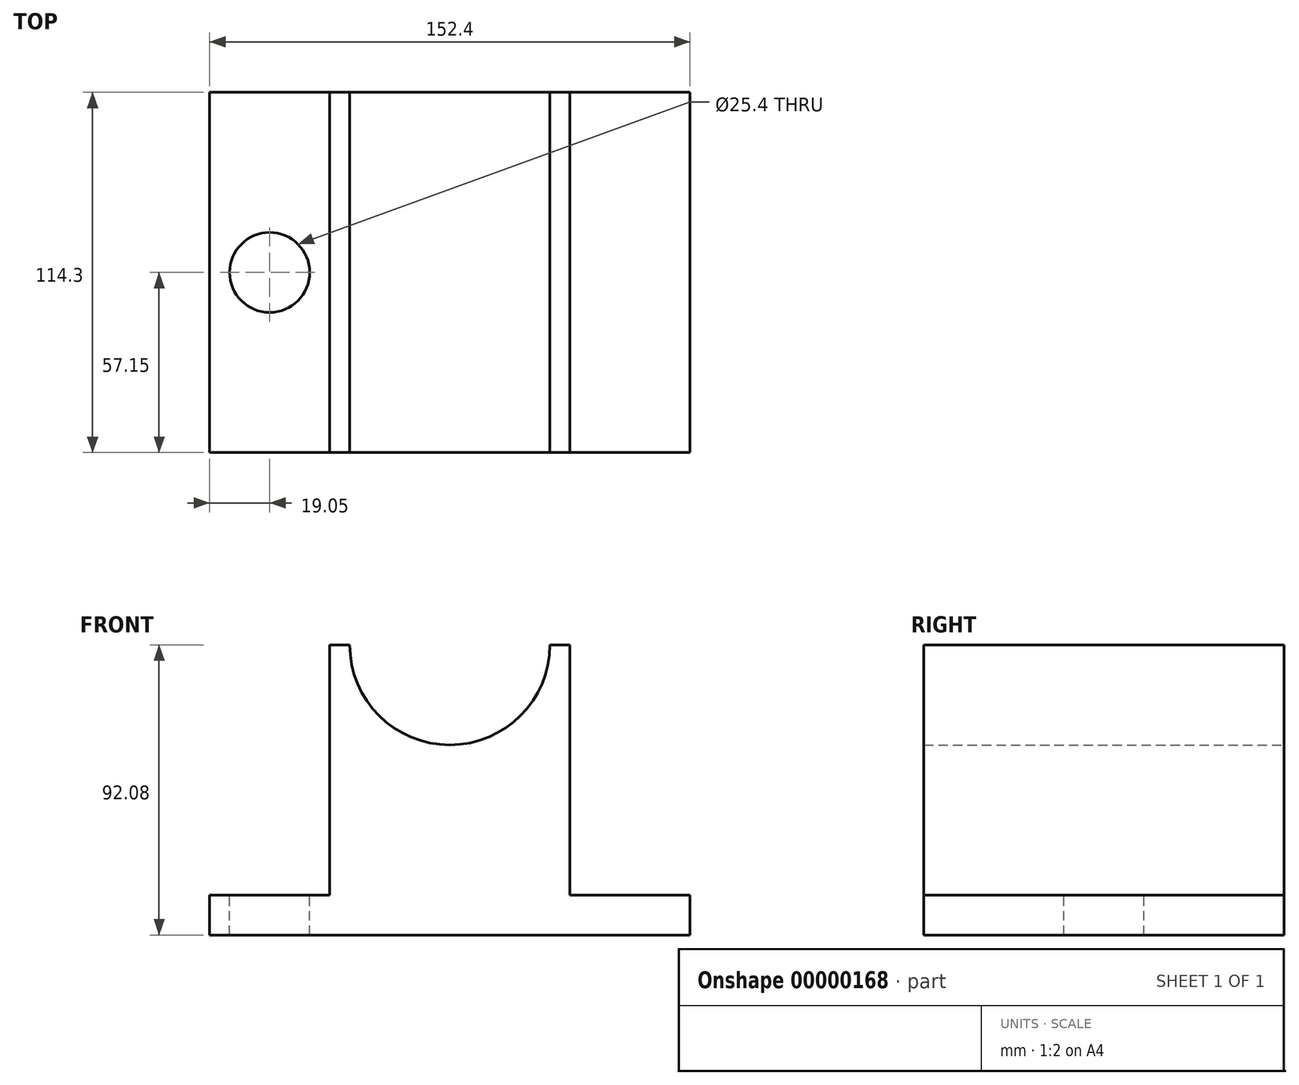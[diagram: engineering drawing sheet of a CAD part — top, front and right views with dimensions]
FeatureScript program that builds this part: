
annotation { "Feature Type Name" : "Feature", "Feature Type Description" : "" }
export const myFeature = defineFeature(function(context is Context, id is Id, definition is map)
    precondition{}
    {
        {
            var Q0;
            Q0=qCreatedBy(makeId("Front.planeOp"),FACE);
            var sketch = newSketch(context, id + "F0", { "sketchPlane" : qUnion([Q0])});
            skLineSegment(sketch, "E0", {"start": v(0, 0) * mm, "end": v(0, 12.7) * mm});
            skLineSegment(sketch, "E1", {"start": v(0, 12.7) * mm, "end": v(38.1, 12.7) * mm});
            skLineSegment(sketch, "E2", {"start": v(38.1, 12.7) * mm, "end": v(38.1, 92.08) * mm});
            skLineSegment(sketch, "E3", {"start": v(38.1, 92.08) * mm, "end": v(44.45, 92.08) * mm});
            skLineSegment(sketch, "E4", {"start": v(114.3, 92.08) * mm, "end": v(114.3, 12.7) * mm});
            skLineSegment(sketch, "E5", {"start": v(114.3, 12.7) * mm, "end": v(152.4, 12.7) * mm});
            skLineSegment(sketch, "E6", {"start": v(152.4, 12.7) * mm, "end": v(152.4, 0) * mm});
            skLineSegment(sketch, "E7", {"start": v(152.4, 0) * mm, "end": v(0, 0) * mm});
            skArc(sketch, "E8", {"start": v(44.45, 92.08) * mm, "mid": v(76.2, 60.33) * mm, "end": v(107.95, 92.08) * mm});
            skLineSegment(sketch, "E9.trimOffspring", {"start": v(107.95, 92.08) * mm, "end": v(114.3, 92.08) * mm});
            skSolve(sketch);
        }
        {
            var Q0;
            Q0=makeQuery(id+"F0.imprint","IMPRINT",FACE,{"disambiguationData":[TD([[makeQuery(id+"F0.imprint","IMPRINT",EDGE,{"derivedFrom":sQuery(id+"F0.wireOp",EDGE,"E0")}),-1.0]])]});
            extrude(context, id + "F1", {"entities" : qUnion([Q0]), "depth" : 114.3 * mm});
        }
        {
            var Q0;
            Q0=makeQuery(id+"F1.opExtrude","SWEPT_FACE",FACE,{"disambiguationData":[OSD([sQuery(id+"F0.wireOp",EDGE,"E1")])]});
            var sketch = newSketch(context, id + "F2", { "sketchPlane" : qUnion([Q0])});
            skCircle(sketch, "E10", {"center": v(19.05, -57.15) * mm, "radius": 12.7 * mm});
            skLineSegment(sketch, "E11.0", {"start": v(107.95, 0) * mm, "end": v(44.45, 0) * mm, "construction": true});
            skLineSegment(sketch, "E12.0", {"start": v(107.95, -114.3) * mm, "end": v(44.45, -114.3) * mm});
            skCircle(sketch, "E13.0.MirrorC", {"center": v(133.35, -57.15) * mm, "radius": 12.7 * mm});
            skSolve(sketch);
        }
        {
            var Q0;
            Q0=makeQuery(id+"F2.imprint","IMPRINT",FACE,{"disambiguationData":[TD([[makeQuery(id+"F2.imprint","IMPRINT",EDGE,{"derivedFrom":sQuery(id+"F2.wireOp",EDGE,"E10")}),1.0]])]});
            var Q1;
            Q1=makeQuery(id+"F2.imprint","IMPRINT",FACE,{"disambiguationData":[TD([[makeQuery(id+"F2.imprint","IMPRINT",EDGE,{"derivedFrom":sQuery(id+"F2.wireOp",EDGE,"E13.0.MirrorC")}),-1.0]])]});
            extrude(context, id + "F3", {"entities" : qUnion([Q0, Q1]), "operationType" : NewBodyOperationType.REMOVE, "endBound" : BoundingType.THROUGH_ALL, "oppositeDirection" : true, "depth" : 25.4 * mm});
        }
    });
